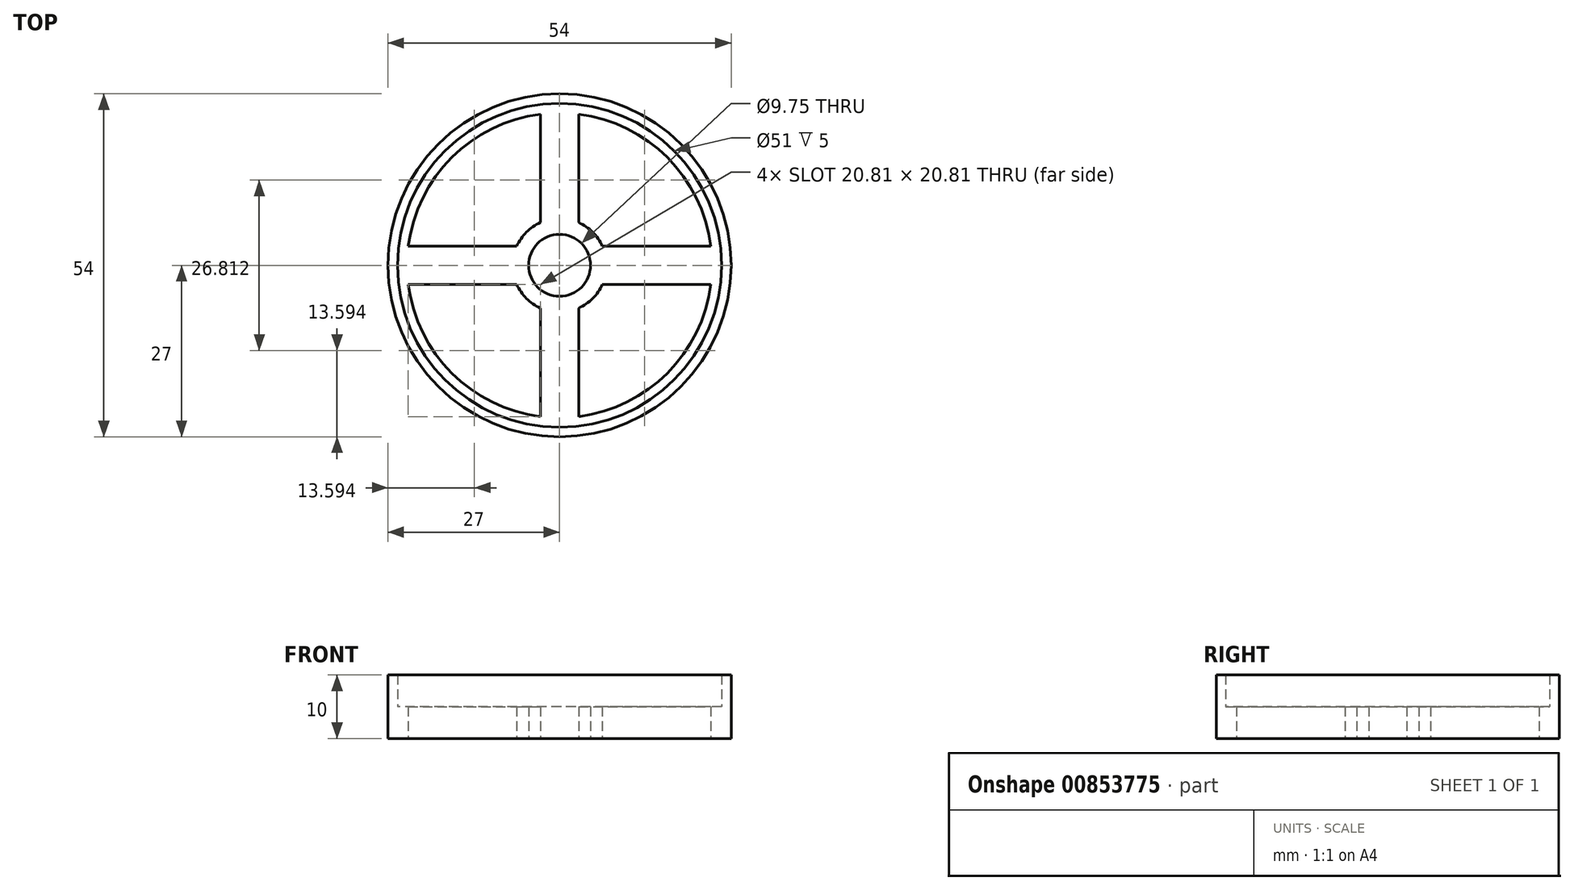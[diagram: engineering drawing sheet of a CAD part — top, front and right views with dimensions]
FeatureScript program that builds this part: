
annotation { "Feature Type Name" : "Feature", "Feature Type Description" : "" }
export const myFeature = defineFeature(function(context is Context, id is Id, definition is map)
    precondition{}
    {
        {
            var Q0;
            Q0=qCreatedBy(makeId("Top.planeOp"),FACE);
            var sketch = newSketch(context, id + "F0", { "sketchPlane" : qUnion([Q0])});
            skCircle(sketch, "E0", {"center": v(0, 0) * mm, "radius": 4.88 * mm});
            skCircle(sketch, "E1", {"center": v(0, 0) * mm, "radius": 24 * mm});
            skCircle(sketch, "E2", {"center": v(0, 0) * mm, "radius": 7.38 * mm});
            skLineSegment(sketch, "E3", {"start": v(0, 7.38) * mm, "end": v(0, 0) * mm});
            skLineSegment(sketch, "E4", {"start": v(0, 0) * mm, "end": v(-7.38, 0) * mm});
            skLineSegment(sketch, "E5", {"start": v(0, 0) * mm, "end": v(7.38, 0) * mm});
            skLineSegment(sketch, "E6", {"start": v(0, 0) * mm, "end": v(0, -7.38) * mm});
            skLineSegment(sketch, "E7", {"start": v(3, -23.81) * mm, "end": v(3, -6.74) * mm});
            skLineSegment(sketch, "E8", {"start": v(-3, -23.81) * mm, "end": v(-3, -6.74) * mm});
            skLineSegment(sketch, "E9", {"start": v(-23.81, -3) * mm, "end": v(-6.74, -3) * mm});
            skLineSegment(sketch, "E10", {"start": v(-3, 23.81) * mm, "end": v(-3, 6.74) * mm});
            skLineSegment(sketch, "E11", {"start": v(3, 23.81) * mm, "end": v(3, 6.74) * mm});
            skLineSegment(sketch, "E12", {"start": v(23.81, 3) * mm, "end": v(6.74, 3) * mm});
            skLineSegment(sketch, "E13", {"start": v(23.81, -3) * mm, "end": v(6.74, -3) * mm});
            skLineSegment(sketch, "E14", {"start": v(-23.81, 3) * mm, "end": v(-6.74, 3) * mm});
            skPoint(sketch, "E15.orphan", {"position": v(0, 24) * mm});
            skLineSegment(sketch, "E16", {"start": v(-3, 23.81) * mm, "end": v(-3, 32.36) * mm});
            skLineSegment(sketch, "E17", {"start": v(3, 23.81) * mm, "end": v(3, 32.36) * mm});
            skLineSegment(sketch, "E18", {"start": v(23.81, 3) * mm, "end": v(32.36, 3) * mm});
            skLineSegment(sketch, "E19", {"start": v(23.81, -3) * mm, "end": v(32.36, -3) * mm});
            skLineSegment(sketch, "E20", {"start": v(3, -23.81) * mm, "end": v(3, -32.36) * mm});
            skLineSegment(sketch, "E21", {"start": v(-3, -23.81) * mm, "end": v(-3, -32.36) * mm});
            skLineSegment(sketch, "E22", {"start": v(-23.81, 3) * mm, "end": v(-32.36, 3) * mm});
            skLineSegment(sketch, "E23", {"start": v(-23.81, -3) * mm, "end": v(-32.36, -3) * mm});
            skCircle(sketch, "E24", {"center": v(0, 0) * mm, "radius": 27 * mm});
            skSolve(sketch);
        }
        {
            var Q0;
            Q0=qSketchRegion(id+"F0",true);
            var Q1;
            {var subQ0=sQuery(id+"F0.wireOp",EDGE,"E9");Q1=makeQuery(id+"F0.imprint","IMPRINT",FACE,{"disambiguationData":[TD([[makeQuery(id+"F0.imprint","IMPRINT",EDGE,{"derivedFrom":subQ0}),1.0]])]});}
            var Q2;
            {var subQ5=sQuery(id+"F0.wireOp",EDGE,"E0");var subQ7=sQuery(id+"F0.wireOp",EDGE,"E3");var subQ9=makeQuery(id+"F0.imprint","INTERSECT",VERTEX,{"derivedFrom":[subQ5,subQ7]});Q2=makeQuery(id+"F0.imprint","IMPRINT",FACE,{"disambiguationData":[TD([[makeQuery(id+"F0.imprint","IMPRINT",EDGE,{"disambiguationData":[TD([[subQ9,-1.0]])],"derivedFrom":subQ5}),-1.0]])]});}
            var Q3;
            {var subQ4=sQuery(id+"F0.wireOp",EDGE,"E0");var subQ7=sQuery(id+"F0.wireOp",EDGE,"E4");var subQ9=makeQuery(id+"F0.imprint","INTERSECT",VERTEX,{"derivedFrom":[subQ4,subQ7]});Q3=makeQuery(id+"F0.imprint","IMPRINT",FACE,{"disambiguationData":[TD([[makeQuery(id+"F0.imprint","IMPRINT",EDGE,{"disambiguationData":[TD([[subQ9,-1.0]])],"derivedFrom":subQ4}),-1.0]])]});}
            var Q4;
            {var subQ0=sQuery(id+"F0.wireOp",EDGE,"E5");var subQ7=sQuery(id+"F0.wireOp",EDGE,"E0");var subQ8=makeQuery(id+"F0.imprint","INTERSECT",VERTEX,{"derivedFrom":[subQ7,subQ0]});Q4=makeQuery(id+"F0.imprint","IMPRINT",FACE,{"disambiguationData":[TD([[makeQuery(id+"F0.imprint","IMPRINT",EDGE,{"disambiguationData":[TD([[subQ8,1.0]])],"derivedFrom":subQ7}),-1.0]])]});}
            var Q5;
            {var subQ3=sQuery(id+"F0.wireOp",EDGE,"E3");var subQ5=sQuery(id+"F0.wireOp",EDGE,"E0");var subQ6=makeQuery(id+"F0.imprint","INTERSECT",VERTEX,{"derivedFrom":[subQ5,subQ3]});Q5=makeQuery(id+"F0.imprint","IMPRINT",FACE,{"disambiguationData":[TD([[makeQuery(id+"F0.imprint","IMPRINT",EDGE,{"disambiguationData":[TD([[subQ6,1.0]])],"derivedFrom":subQ5}),-1.0]])]});}
            var Q6;
            {var subQ3=sQuery(id+"F0.wireOp",EDGE,"E10");Q6=makeQuery(id+"F0.imprint","IMPRINT",FACE,{"disambiguationData":[TD([[makeQuery(id+"F0.imprint","IMPRINT",EDGE,{"derivedFrom":subQ3}),1.0]])]});}
            var Q7;
            {var subQ3=sQuery(id+"F0.wireOp",EDGE,"E12");Q7=makeQuery(id+"F0.imprint","IMPRINT",FACE,{"disambiguationData":[TD([[makeQuery(id+"F0.imprint","IMPRINT",EDGE,{"derivedFrom":subQ3}),1.0]])]});}
            var Q8;
            {var subQ0=sQuery(id+"F0.wireOp",EDGE,"E7");Q8=makeQuery(id+"F0.imprint","IMPRINT",FACE,{"disambiguationData":[TD([[makeQuery(id+"F0.imprint","IMPRINT",EDGE,{"derivedFrom":subQ0}),1.0]])]});}
            var Q9;
            {var subQ0=sQuery(id+"F0.wireOp",EDGE,"E16");Q9=makeQuery(id+"F0.imprint","IMPRINT",FACE,{"disambiguationData":[TD([[makeQuery(id+"F0.imprint","IMPRINT",EDGE,{"derivedFrom":subQ0}),-1.0]])]});}
            var Q10;
            {var subQ0=sQuery(id+"F0.wireOp",EDGE,"E18");Q10=makeQuery(id+"F0.imprint","IMPRINT",FACE,{"disambiguationData":[TD([[makeQuery(id+"F0.imprint","IMPRINT",EDGE,{"derivedFrom":subQ0}),-1.0]])]});}
            var Q11;
            {var subQ2=sQuery(id+"F0.wireOp",EDGE,"E22");Q11=makeQuery(id+"F0.imprint","IMPRINT",FACE,{"disambiguationData":[TD([[makeQuery(id+"F0.imprint","IMPRINT",EDGE,{"derivedFrom":subQ2}),1.0]])]});}
            var Q12;
            {var subQ0=sQuery(id+"F0.wireOp",EDGE,"E20");Q12=makeQuery(id+"F0.imprint","IMPRINT",FACE,{"disambiguationData":[TD([[makeQuery(id+"F0.imprint","IMPRINT",EDGE,{"derivedFrom":subQ0}),-1.0]])]});}
            var Q13;
            {var subQ0=sQuery(id+"F0.wireOp",EDGE,"xLouXmni-Sbui-ifnC-rC28-wyGckixbnfYQ");var subQ1=sQuery(id+"F0.wireOp",EDGE,"E16");var subQ2=makeQuery(id+"F0.imprint","INTERSECT",VERTEX,{"derivedFrom":[subQ1,subQ0]});Q13=makeQuery(id+"F0.imprint","IMPRINT",FACE,{"disambiguationData":[TD([[makeQuery(id+"F0.imprint","IMPRINT",EDGE,{"disambiguationData":[TD([[subQ2,-1.0]])],"derivedFrom":subQ1}),1.0]])]});}
            var Q14;
            {var subQ0=sQuery(id+"F0.wireOp",EDGE,"xLouXmni-Sbui-ifnC-rC28-wyGckixbnfYQ");var subQ1=sQuery(id+"F0.wireOp",EDGE,"E17");var subQ2=makeQuery(id+"F0.imprint","INTERSECT",VERTEX,{"derivedFrom":[subQ1,subQ0]});Q14=makeQuery(id+"F0.imprint","IMPRINT",FACE,{"disambiguationData":[TD([[makeQuery(id+"F0.imprint","IMPRINT",EDGE,{"disambiguationData":[TD([[subQ2,-1.0]])],"derivedFrom":subQ1}),-1.0]])]});}
            var Q15;
            {var subQ0=sQuery(id+"F0.wireOp",EDGE,"xLouXmni-Sbui-ifnC-rC28-wyGckixbnfYQ");var subQ1=sQuery(id+"F0.wireOp",EDGE,"E19");var subQ2=makeQuery(id+"F0.imprint","INTERSECT",VERTEX,{"derivedFrom":[subQ1,subQ0]});Q15=makeQuery(id+"F0.imprint","IMPRINT",FACE,{"disambiguationData":[TD([[makeQuery(id+"F0.imprint","IMPRINT",EDGE,{"disambiguationData":[TD([[subQ2,-1.0]])],"derivedFrom":subQ1}),-1.0]])]});}
            var Q16;
            {var subQ0=sQuery(id+"F0.wireOp",EDGE,"xLouXmni-Sbui-ifnC-rC28-wyGckixbnfYQ");var subQ1=sQuery(id+"F0.wireOp",EDGE,"E21");var subQ2=makeQuery(id+"F0.imprint","INTERSECT",VERTEX,{"derivedFrom":[subQ1,subQ0]});Q16=makeQuery(id+"F0.imprint","IMPRINT",FACE,{"disambiguationData":[TD([[makeQuery(id+"F0.imprint","IMPRINT",EDGE,{"disambiguationData":[TD([[subQ2,-1.0]])],"derivedFrom":subQ1}),-1.0]])]});}
            extrude(context, id + "F1", {"entities" : qUnion([Q0, Q1, Q2, Q3, Q4, Q5, Q6, Q7, Q8, Q9, Q10, Q11, Q12, Q13, Q14, Q15, Q16]), "depth" : 5 * mm, "offsetDistance" : 25 * mm});
        }
        {
            var Q0;
            Q0=makeQuery(id+"F1.opExtrude","CAP_FACE",FACE,{"disambiguationData":[OSD([sQuery(id+"F0.wireOp",EDGE,"E0"),sQuery(id+"F0.wireOp",EDGE,"sDJ0dak9-lFHa-rwrc-QJoe-sjPW8o3cdHDN")])],"isStart":false});
            var sketch = newSketch(context, id + "F2", { "sketchPlane" : qUnion([Q0])});
            skCircle(sketch, "E25", {"center": v(0, 0) * mm, "radius": 27 * mm});
            skCircle(sketch, "E26", {"center": v(0, 0) * mm, "radius": 25.5 * mm});
            skSolve(sketch);
        }
        {
            var Q0;
            Q0=qSketchRegion(id+"F2",true);
            extrude(context, id + "F3", {"entities" : qUnion([Q0]), "operationType" : NewBodyOperationType.ADD, "depth" : 5 * mm, "offsetDistance" : 25 * mm});
        }
    });
